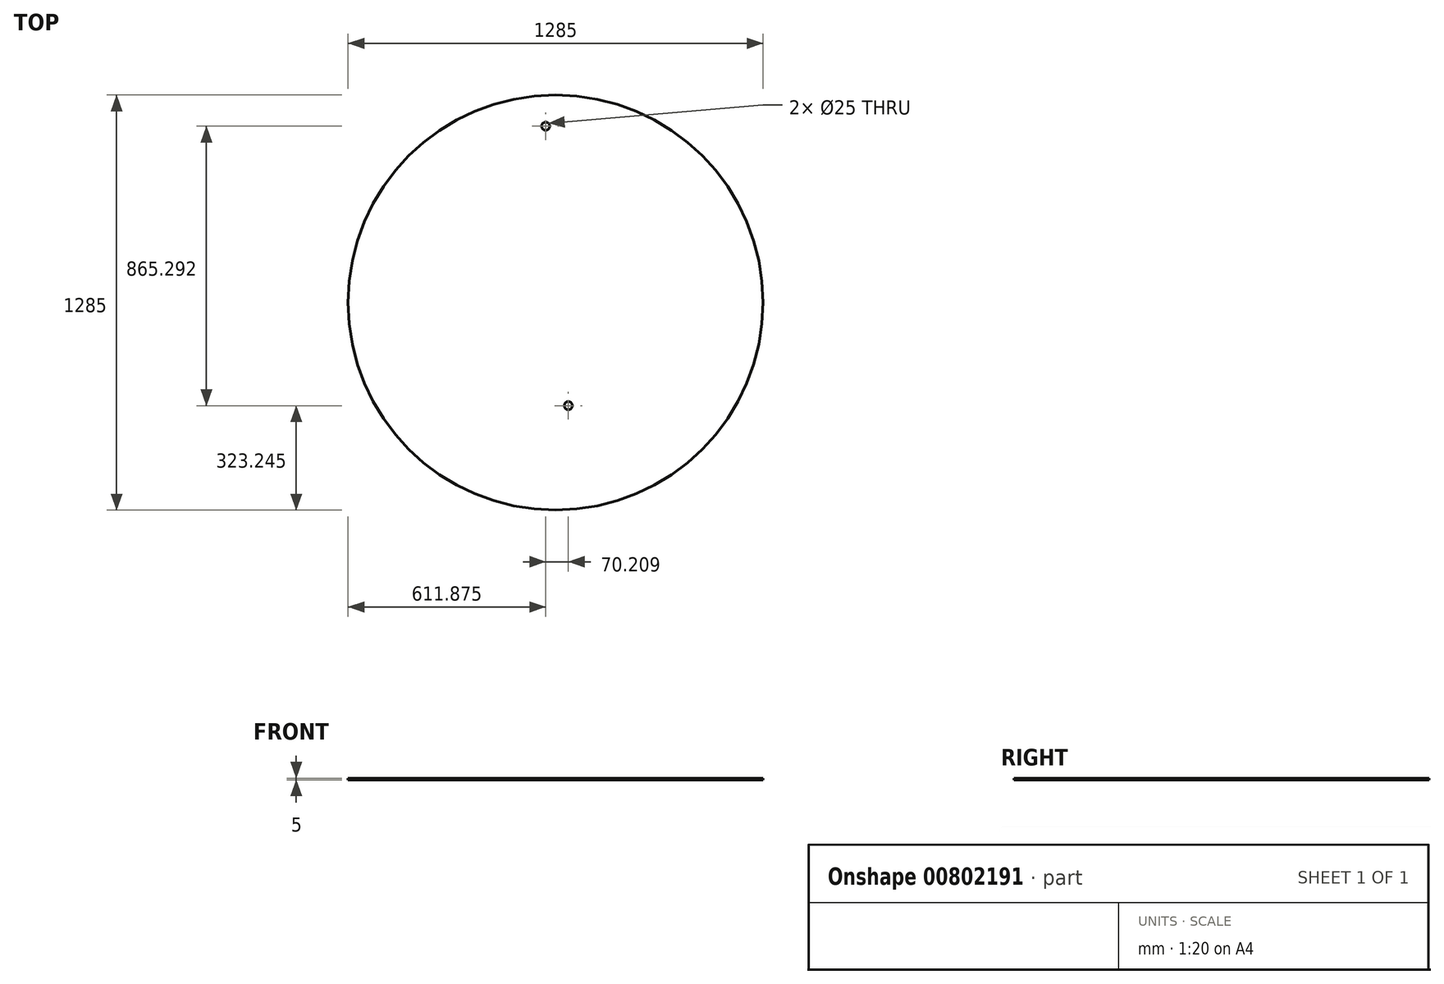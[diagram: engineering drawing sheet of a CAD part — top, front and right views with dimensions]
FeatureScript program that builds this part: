
annotation { "Feature Type Name" : "Feature", "Feature Type Description" : "" }
export const myFeature = defineFeature(function(context is Context, id is Id, definition is map)
    precondition{}
    {
        {
            var Q0;
            Q0=qCreatedBy(makeId("Top.planeOp"),FACE);
            var sketch = newSketch(context, id + "F0", { "sketchPlane" : qUnion([Q0])});
            skCircle(sketch, "E0", {"center": v(0, 0) * mm, "radius": 642.5 * mm});
            skCircle(sketch, "E1", {"center": v(-30.63, 546.04) * mm, "radius": 12.5 * mm});
            skCircle(sketch, "E2", {"center": v(39.58, -319.26) * mm, "radius": 12.5 * mm});
            skSolve(sketch);
        }
        {
            var Q0;
            Q0=makeQuery(id+"F0.imprint","IMPRINT",FACE,{"disambiguationData":[TD([[makeQuery(id+"F0.imprint","IMPRINT",EDGE,{"derivedFrom":sQuery(id+"F0.wireOp",EDGE,"E0")}),1.0]])]});
            extrude(context, id + "F1", {"entities" : qUnion([Q0]), "depth" : 5 * mm, "offsetDistance" : 25 * mm});
        }
    });
